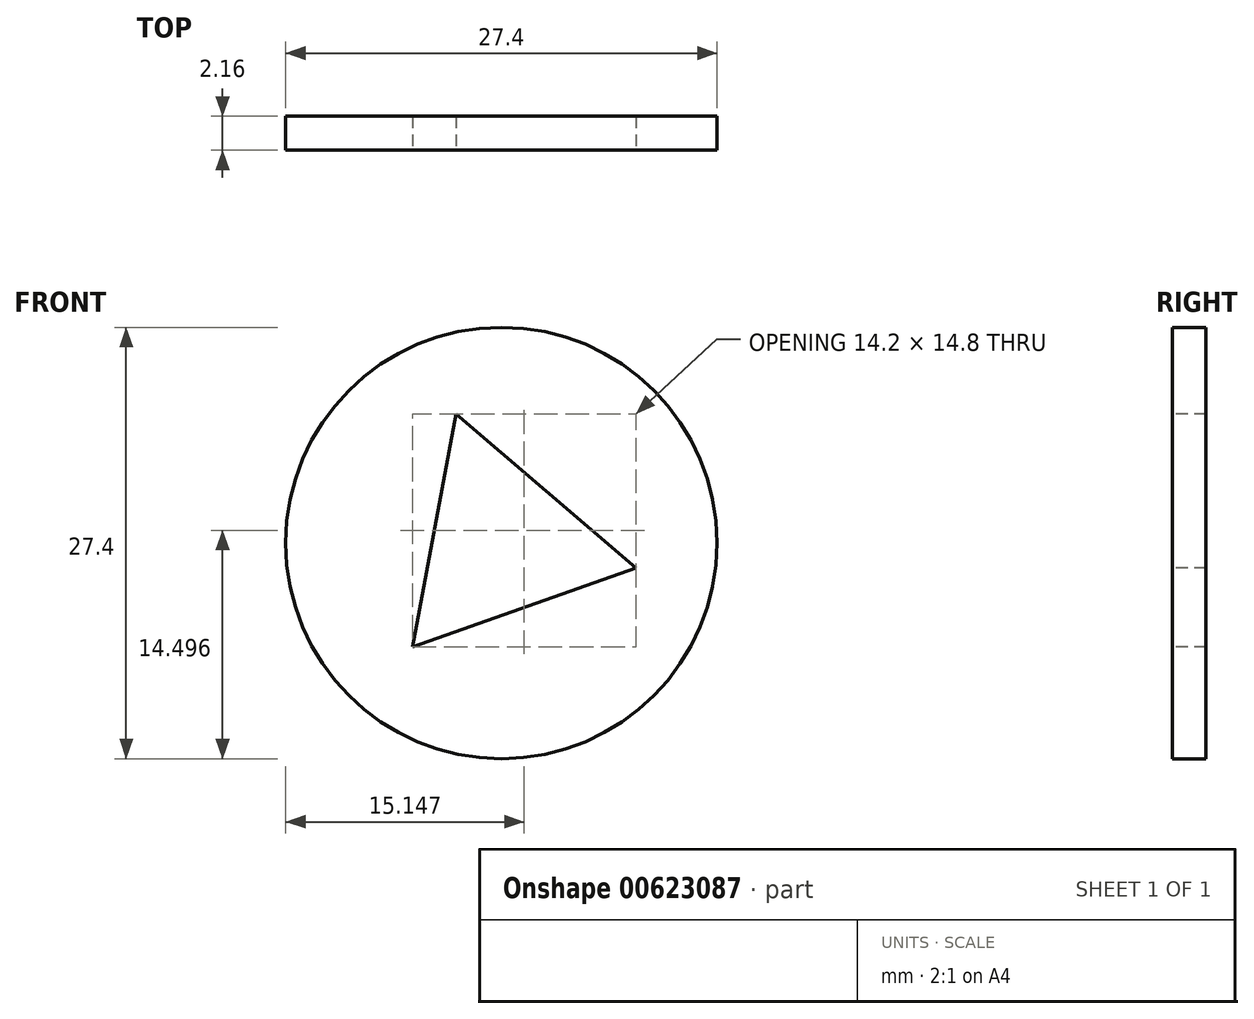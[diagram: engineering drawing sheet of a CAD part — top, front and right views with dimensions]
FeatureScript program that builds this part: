
annotation { "Feature Type Name" : "Feature", "Feature Type Description" : "" }
export const myFeature = defineFeature(function(context is Context, id is Id, definition is map)
    precondition{}
    {
        {
            var Q0;
            Q0=qCreatedBy(makeId("Front.planeOp"),FACE);
            var sketch = newSketch(context, id + "F0", { "sketchPlane" : qUnion([Q0])});
            skCircle(sketch, "E0", {"center": v(0, 0) * mm, "radius": 13.7 * mm});
            skSolve(sketch);
        }
        {
            var Q0;
            Q0=makeQuery(id+"F0.imprint","IMPRINT",FACE,{"disambiguationData":[TD([[makeQuery(id+"F0.imprint","IMPRINT",EDGE,{"derivedFrom":sQuery(id+"F0.wireOp",EDGE,"E0")}),1.0]])]});
            extrude(context, id + "F1", {"entities" : qUnion([Q0]), "endBound" : BoundingType.SYMMETRIC, "depth" : 2.15 * mm, "offsetDistance" : 25 * mm});
        }
        {
            var Q0;
            Q0=makeQuery(id+"F1.opExtrude","CAP_FACE",FACE,{"disambiguationData":[OSD([sQuery(id+"F0.wireOp",EDGE,"E0")])],"isStart":false});
            var sketch = newSketch(context, id + "F2", { "sketchPlane" : qUnion([Q0])});
            skCircle(sketch, "E1.cCircle", {"center": v(0, 0) * mm, "radius": 4.35 * mm, "construction": true});
            skLineSegment(sketch, "E1.0", {"start": v(8.54, -1.6) * mm, "end": v(-5.65, -6.6) * mm});
            skLineSegment(sketch, "E1.1", {"start": v(-5.65, -6.6) * mm, "end": v(-2.9, 8.2) * mm});
            skLineSegment(sketch, "E1.2", {"start": v(-2.9, 8.2) * mm, "end": v(8.54, -1.6) * mm});
            skPoint(sketch, "E1.0.midPoint", {"position": v(1.45, -4.1) * mm});
            skSolve(sketch);
        }
        {
            var Q0;
            Q0=makeQuery(id+"F2.imprint","IMPRINT",FACE,{"disambiguationData":[TD([[makeQuery(id+"F2.imprint","IMPRINT",EDGE,{"derivedFrom":sQuery(id+"F2.wireOp",EDGE,"E1.0")}),-1.0]])]});
            extrude(context, id + "F3", {"entities" : qUnion([Q0]), "operationType" : NewBodyOperationType.REMOVE, "endBound" : BoundingType.UP_TO_NEXT, "oppositeDirection" : true, "depth" : 25 * mm, "offsetDistance" : 25 * mm});
        }
    });
